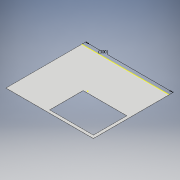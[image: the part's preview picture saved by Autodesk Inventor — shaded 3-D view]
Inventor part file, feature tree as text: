
AUTODESK INVENTOR PART (.ipt)
format: ipt  version: 2017 (Build 210142000, 142)  size: 111,104 bytes
history: native  units: mm
features: sketch x3, other x2, sheet_metal_op x1
ambient origin geometry x8: Origin, YZ Plane, XZ Plane, XY Plane, X Axis, Y Axis, Z Axis, Center Point
bodies: Solid1 (feature_tree)
feature tree (6):
  sheet_metal_op  "Face1"
  sketch  "Sketch4"  dims[d2=0.5mm d3=280.0mm d4=240.0mm d5=150.0mm d6=115.0mm d7=0.5mm d8=0.0mm d9=300.0mm]
  sketch  "Sketch1"  dims[d0=300.0mm]
  other  "Plate1"
  sketch  "Sketch3"  dims[d1=260.0mm]
  other  "Cut1"
